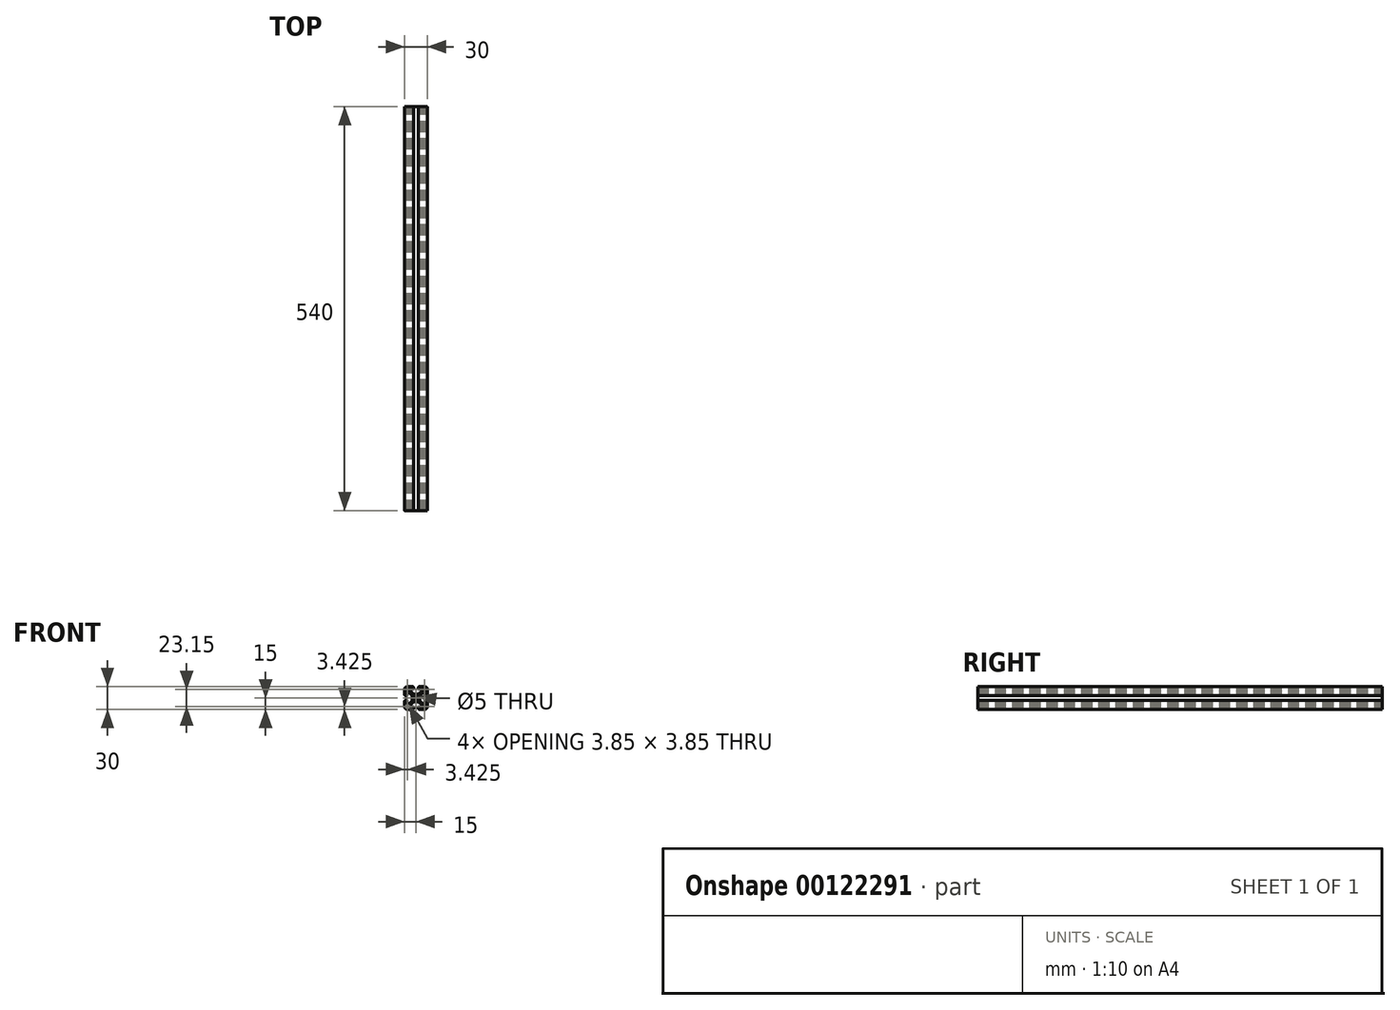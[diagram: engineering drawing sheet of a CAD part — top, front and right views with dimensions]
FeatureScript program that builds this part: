
annotation { "Feature Type Name" : "Feature", "Feature Type Description" : "" }
export const myFeature = defineFeature(function(context is Context, id is Id, definition is map)
    precondition{}
    {
        {
            var Q0;
            Q0=qCreatedBy(makeId("Front.planeOp"),FACE);
            var sketch = newSketch(context, id + "F0", { "sketchPlane" : qUnion([Q0])});
            skLineSegment(sketch, "E0", {"start": v(0, 5.25) * mm, "end": v(2.6, 5.25) * mm});
            skLineSegment(sketch, "E1", {"start": v(4.71, 6.13) * mm, "end": v(7.27, 8.69) * mm});
            skLineSegment(sketch, "E2", {"start": v(8.15, 10.8) * mm, "end": v(8.15, 12.5) * mm});
            skLineSegment(sketch, "E3", {"start": v(7.15, 13.5) * mm, "end": v(5.9, 13.5) * mm});
            skLineSegment(sketch, "E4", {"start": v(5.6, 13.2) * mm, "end": v(5.6, 12.3) * mm});
            skLineSegment(sketch, "E5", {"start": v(5.3, 12) * mm, "end": v(3.9, 12) * mm});
            skLineSegment(sketch, "E6", {"start": v(3.1, 12.8) * mm, "end": v(3.1, 14) * mm});
            skLineSegment(sketch, "E7", {"start": v(4.1, 15) * mm, "end": v(12, 15) * mm});
            skPoint(sketch, "E8.visualSharp", {"position": v(3.84, 5.25) * mm});
            skArc(sketch, "E8.filletArc", {"start": v(2.6, 5.25) * mm, "mid": v(3.74, 5.48) * mm, "end": v(4.71, 6.13) * mm});
            skPoint(sketch, "E9.visualSharp", {"position": v(8.15, 9.56) * mm});
            skArc(sketch, "E9.filletArc", {"start": v(7.27, 8.69) * mm, "mid": v(7.92, 9.66) * mm, "end": v(8.15, 10.8) * mm});
            skPoint(sketch, "E10.visualSharp", {"position": v(8.15, 13.5) * mm});
            skArc(sketch, "E10.filletArc", {"start": v(8.15, 12.5) * mm, "mid": v(7.86, 13.2) * mm, "end": v(7.15, 13.5) * mm});
            skPoint(sketch, "E11.visualSharp", {"position": v(5.6, 13.5) * mm});
            skArc(sketch, "E11.filletArc", {"start": v(5.9, 13.5) * mm, "mid": v(5.69, 13.41) * mm, "end": v(5.6, 13.2) * mm});
            skPoint(sketch, "E12.visualSharp", {"position": v(5.6, 12) * mm});
            skArc(sketch, "E12.filletArc", {"start": v(5.3, 12) * mm, "mid": v(5.51, 12.09) * mm, "end": v(5.6, 12.3) * mm});
            skPoint(sketch, "E13.visualSharp", {"position": v(3.1, 12) * mm});
            skArc(sketch, "E13.filletArc", {"start": v(3.1, 12.8) * mm, "mid": v(3.33, 12.23) * mm, "end": v(3.9, 12) * mm});
            skPoint(sketch, "E14.visualSharp", {"position": v(3.1, 15) * mm});
            skArc(sketch, "E14.filletArc", {"start": v(4.1, 15) * mm, "mid": v(3.4, 14.7) * mm, "end": v(3.1, 14) * mm});
            skArc(sketch, "E15.MirrorCS", {"start": v(12, 5.3) * mm, "mid": v(12.09, 5.51) * mm, "end": v(12.3, 5.6) * mm});
            skArc(sketch, "E16.MirrorCS", {"start": v(13.5, 5.9) * mm, "mid": v(13.41, 5.69) * mm, "end": v(13.2, 5.6) * mm});
            skPoint(sketch, "E17.MirrorP", {"position": v(13.5, 5.6) * mm});
            skLineSegment(sketch, "E18.MirrorCS", {"start": v(5.25, 0) * mm, "end": v(5.25, 2.6) * mm});
            skLineSegment(sketch, "E19.MirrorCS", {"start": v(6.13, 4.71) * mm, "end": v(8.69, 7.27) * mm});
            skPoint(sketch, "E20.MirrorP", {"position": v(13.5, 8.15) * mm});
            skLineSegment(sketch, "E21.MirrorCS", {"start": v(10.8, 8.15) * mm, "end": v(12.5, 8.15) * mm});
            skLineSegment(sketch, "E22.MirrorCS", {"start": v(13.5, 7.15) * mm, "end": v(13.5, 5.9) * mm});
            skPoint(sketch, "E23.MirrorP", {"position": v(9.56, 8.15) * mm});
            skLineSegment(sketch, "E24.MirrorCS", {"start": v(13.2, 5.6) * mm, "end": v(12.3, 5.6) * mm});
            skArc(sketch, "E25.MirrorCS", {"start": v(15, 4.1) * mm, "mid": v(14.7, 3.4) * mm, "end": v(14, 3.1) * mm});
            skArc(sketch, "E26.MirrorCS", {"start": v(12.8, 3.1) * mm, "mid": v(12.23, 3.33) * mm, "end": v(12, 3.9) * mm});
            skPoint(sketch, "E27.MirrorP", {"position": v(12, 5.6) * mm});
            skLineSegment(sketch, "E28.MirrorCS", {"start": v(12, 5.3) * mm, "end": v(12, 3.9) * mm});
            skPoint(sketch, "E29.MirrorP", {"position": v(5.25, 3.84) * mm});
            skLineSegment(sketch, "E30.MirrorCS", {"start": v(15, 4.1) * mm, "end": v(15, 12) * mm});
            skLineSegment(sketch, "E31.MirrorCS", {"start": v(12.8, 3.1) * mm, "end": v(14, 3.1) * mm});
            skArc(sketch, "E32.MirrorCS", {"start": v(5.25, 2.6) * mm, "mid": v(5.48, 3.74) * mm, "end": v(6.13, 4.71) * mm});
            skArc(sketch, "E33.MirrorCS", {"start": v(12.5, 8.15) * mm, "mid": v(13.2, 7.86) * mm, "end": v(13.5, 7.15) * mm});
            skArc(sketch, "E34.MirrorCS", {"start": v(8.69, 7.27) * mm, "mid": v(9.66, 7.92) * mm, "end": v(10.8, 8.15) * mm});
            skPoint(sketch, "E35.MirrorP", {"position": v(15, 3.1) * mm});
            skPoint(sketch, "E36.MirrorP", {"position": v(12, 3.1) * mm});
            skArc(sketch, "E37.MirrorCS", {"start": v(-5.9, 13.5) * mm, "mid": v(-5.69, 13.41) * mm, "end": v(-5.6, 13.2) * mm});
            skLineSegment(sketch, "E38.MirrorCS", {"start": v(-5.6, 13.2) * mm, "end": v(-5.6, 12.3) * mm});
            skArc(sketch, "E39.MirrorCS", {"start": v(-5.3, 12) * mm, "mid": v(-5.51, 12.09) * mm, "end": v(-5.6, 12.3) * mm});
            skArc(sketch, "E40.MirrorCS", {"start": v(-12, 5.3) * mm, "mid": v(-12.09, 5.51) * mm, "end": v(-12.3, 5.6) * mm});
            skLineSegment(sketch, "E41.MirrorCS", {"start": v(-13.2, 5.6) * mm, "end": v(-12.3, 5.6) * mm});
            skArc(sketch, "E42.MirrorCS", {"start": v(-13.5, 5.9) * mm, "mid": v(-13.41, 5.69) * mm, "end": v(-13.2, 5.6) * mm});
            skArc(sketch, "E43.MirrorCS", {"start": v(-12.5, 8.15) * mm, "mid": v(-13.2, 7.86) * mm, "end": v(-13.5, 7.15) * mm});
            skArc(sketch, "E44.MirrorCS", {"start": v(-15, 4.1) * mm, "mid": v(-14.7, 3.4) * mm, "end": v(-14, 3.1) * mm});
            skArc(sketch, "E45.MirrorCS", {"start": v(-8.15, 12.5) * mm, "mid": v(-7.86, 13.2) * mm, "end": v(-7.15, 13.5) * mm});
            skLineSegment(sketch, "E46.MirrorCS", {"start": v(-5.3, 12) * mm, "end": v(-3.9, 12) * mm});
            skLineSegment(sketch, "E47.MirrorCS", {"start": v(-7.15, 13.5) * mm, "end": v(-5.9, 13.5) * mm});
            skArc(sketch, "E48.MirrorCS", {"start": v(-3.1, 12.8) * mm, "mid": v(-3.33, 12.23) * mm, "end": v(-3.9, 12) * mm});
            skArc(sketch, "E49.MirrorCS", {"start": v(-4.1, 15) * mm, "mid": v(-3.4, 14.7) * mm, "end": v(-3.1, 14) * mm});
            skArc(sketch, "E50.MirrorCS", {"start": v(-12.8, 3.1) * mm, "mid": v(-12.23, 3.33) * mm, "end": v(-12, 3.9) * mm});
            skPoint(sketch, "E51.MirrorP", {"position": v(-12, 3.1) * mm});
            skLineSegment(sketch, "E52.MirrorCS", {"start": v(-5.25, 0) * mm, "end": v(-5.25, 2.6) * mm});
            skLineSegment(sketch, "E53.MirrorCS", {"start": v(-10.8, 8.15) * mm, "end": v(-12.5, 8.15) * mm});
            skPoint(sketch, "E54.MirrorP", {"position": v(-9.56, 8.15) * mm});
            skLineSegment(sketch, "E55.MirrorCS", {"start": v(-12, 5.3) * mm, "end": v(-12, 3.9) * mm});
            skLineSegment(sketch, "E56.MirrorCS", {"start": v(-12.8, 3.1) * mm, "end": v(-14, 3.1) * mm});
            skArc(sketch, "E57.MirrorCS", {"start": v(-7.27, 8.69) * mm, "mid": v(-7.92, 9.66) * mm, "end": v(-8.15, 10.8) * mm});
            skArc(sketch, "E58.MirrorCS", {"start": v(-2.6, 5.25) * mm, "mid": v(-3.74, 5.48) * mm, "end": v(-4.71, 6.13) * mm});
            skLineSegment(sketch, "E59.MirrorCS", {"start": v(-4.1, 15) * mm, "end": v(-12, 15) * mm});
            skLineSegment(sketch, "E60.MirrorCS", {"start": v(-3.1, 12.8) * mm, "end": v(-3.1, 14) * mm});
            skPoint(sketch, "E61.MirrorP", {"position": v(-8.15, 9.56) * mm});
            skPoint(sketch, "E62.MirrorP", {"position": v(-8.15, 13.5) * mm});
            skPoint(sketch, "E63.MirrorP", {"position": v(-5.25, 3.84) * mm});
            skLineSegment(sketch, "E64.MirrorCS", {"start": v(-8.15, 10.8) * mm, "end": v(-8.15, 12.5) * mm});
            skPoint(sketch, "E65.MirrorP", {"position": v(-15, 3.1) * mm});
            skPoint(sketch, "E66.MirrorP", {"position": v(-5.6, 13.5) * mm});
            skPoint(sketch, "E67.MirrorP", {"position": v(-3.1, 15) * mm});
            skLineSegment(sketch, "E68.MirrorCS", {"start": v(-6.13, 4.71) * mm, "end": v(-8.69, 7.27) * mm});
            skLineSegment(sketch, "E69.MirrorCS", {"start": v(-4.71, 6.13) * mm, "end": v(-7.27, 8.69) * mm});
            skArc(sketch, "E70.MirrorCS", {"start": v(-8.69, 7.27) * mm, "mid": v(-9.66, 7.92) * mm, "end": v(-10.8, 8.15) * mm});
            skLineSegment(sketch, "E71.MirrorCS", {"start": v(-13.5, 7.15) * mm, "end": v(-13.5, 5.9) * mm});
            skPoint(sketch, "E72.MirrorP", {"position": v(-13.5, 8.15) * mm});
            skPoint(sketch, "E73.MirrorP", {"position": v(-3.1, 12) * mm});
            skPoint(sketch, "E74.MirrorP", {"position": v(-3.84, 5.25) * mm});
            skPoint(sketch, "E75.MirrorP", {"position": v(-5.6, 12) * mm});
            skLineSegment(sketch, "E76.MirrorCS", {"start": v(0, 5.25) * mm, "end": v(-2.6, 5.25) * mm});
            skLineSegment(sketch, "E77.MirrorCS", {"start": v(-15, 4.1) * mm, "end": v(-15, 12) * mm});
            skArc(sketch, "E78.MirrorCS", {"start": v(-5.25, 2.6) * mm, "mid": v(-5.48, 3.74) * mm, "end": v(-6.13, 4.71) * mm});
            skPoint(sketch, "E79.MirrorP", {"position": v(-12, 5.6) * mm});
            skPoint(sketch, "E80.MirrorP", {"position": v(-13.5, 5.6) * mm});
            skLineSegment(sketch, "E81.MirrorCS", {"start": v(5.6, -13.2) * mm, "end": v(5.6, -12.3) * mm});
            skArc(sketch, "E82.MirrorCS", {"start": v(5.9, -13.5) * mm, "mid": v(5.69, -13.41) * mm, "end": v(5.6, -13.2) * mm});
            skArc(sketch, "E83.MirrorCS", {"start": v(5.3, -12) * mm, "mid": v(5.51, -12.09) * mm, "end": v(5.6, -12.3) * mm});
            skArc(sketch, "E84.MirrorCS", {"start": v(-12, -5.3) * mm, "mid": v(-12.09, -5.51) * mm, "end": v(-12.3, -5.6) * mm});
            skArc(sketch, "E85.MirrorCS", {"start": v(-5.9, -13.5) * mm, "mid": v(-5.69, -13.41) * mm, "end": v(-5.6, -13.2) * mm});
            skLineSegment(sketch, "E86.MirrorCS", {"start": v(13.2, -5.6) * mm, "end": v(12.3, -5.6) * mm});
            skArc(sketch, "E87.MirrorCS", {"start": v(-5.3, -12) * mm, "mid": v(-5.51, -12.09) * mm, "end": v(-5.6, -12.3) * mm});
            skArc(sketch, "E88.MirrorCS", {"start": v(13.5, -5.9) * mm, "mid": v(13.41, -5.69) * mm, "end": v(13.2, -5.6) * mm});
            skLineSegment(sketch, "E89.MirrorCS", {"start": v(-5.6, -13.2) * mm, "end": v(-5.6, -12.3) * mm});
            skArc(sketch, "E90.MirrorCS", {"start": v(-13.5, -5.9) * mm, "mid": v(-13.41, -5.69) * mm, "end": v(-13.2, -5.6) * mm});
            skArc(sketch, "E91.MirrorCS", {"start": v(12, -5.3) * mm, "mid": v(12.09, -5.51) * mm, "end": v(12.3, -5.6) * mm});
            skLineSegment(sketch, "E92.MirrorCS", {"start": v(-13.2, -5.6) * mm, "end": v(-12.3, -5.6) * mm});
            skArc(sketch, "E93.MirrorCS", {"start": v(-15, -4.1) * mm, "mid": v(-14.7, -3.4) * mm, "end": v(-14, -3.1) * mm});
            skArc(sketch, "E94.MirrorCS", {"start": v(-12.5, -8.15) * mm, "mid": v(-13.2, -7.86) * mm, "end": v(-13.5, -7.15) * mm});
            skArc(sketch, "E95.MirrorCS", {"start": v(12.8, -3.1) * mm, "mid": v(12.23, -3.33) * mm, "end": v(12, -3.9) * mm});
            skArc(sketch, "E96.MirrorCS", {"start": v(-12.8, -3.1) * mm, "mid": v(-12.23, -3.33) * mm, "end": v(-12, -3.9) * mm});
            skLineSegment(sketch, "E97.MirrorCS", {"start": v(7.15, -13.5) * mm, "end": v(5.9, -13.5) * mm});
            skLineSegment(sketch, "E98.MirrorCS", {"start": v(5.3, -12) * mm, "end": v(3.9, -12) * mm});
            skArc(sketch, "E99.MirrorCS", {"start": v(8.15, -12.5) * mm, "mid": v(7.86, -13.2) * mm, "end": v(7.15, -13.5) * mm});
            skArc(sketch, "E100.MirrorCS", {"start": v(-4.1, -15) * mm, "mid": v(-3.4, -14.7) * mm, "end": v(-3.1, -14) * mm});
            skArc(sketch, "E101.MirrorCS", {"start": v(-3.1, -12.8) * mm, "mid": v(-3.33, -12.23) * mm, "end": v(-3.9, -12) * mm});
            skArc(sketch, "E102.MirrorCS", {"start": v(15, -4.1) * mm, "mid": v(14.7, -3.4) * mm, "end": v(14, -3.1) * mm});
            skArc(sketch, "E103.MirrorCS", {"start": v(-8.15, -12.5) * mm, "mid": v(-7.86, -13.2) * mm, "end": v(-7.15, -13.5) * mm});
            skArc(sketch, "E104.MirrorCS", {"start": v(12.5, -8.15) * mm, "mid": v(13.2, -7.86) * mm, "end": v(13.5, -7.15) * mm});
            skArc(sketch, "E105.MirrorCS", {"start": v(3.1, -12.8) * mm, "mid": v(3.33, -12.23) * mm, "end": v(3.9, -12) * mm});
            skArc(sketch, "E106.MirrorCS", {"start": v(4.1, -15) * mm, "mid": v(3.4, -14.7) * mm, "end": v(3.1, -14) * mm});
            skPoint(sketch, "E107.MirrorP", {"position": v(-3.1, -15) * mm});
            skArc(sketch, "E108.MirrorCS", {"start": v(-2.6, -5.25) * mm, "mid": v(-3.74, -5.48) * mm, "end": v(-4.71, -6.13) * mm});
            skLineSegment(sketch, "E109.MirrorCS", {"start": v(5.25, 0) * mm, "end": v(5.25, -2.6) * mm});
            skLineSegment(sketch, "E110.MirrorCS", {"start": v(-6.13, -4.71) * mm, "end": v(-8.69, -7.27) * mm});
            skLineSegment(sketch, "E111.MirrorCS", {"start": v(-12, -5.3) * mm, "end": v(-12, -3.9) * mm});
            skLineSegment(sketch, "E112.MirrorCS", {"start": v(12, -5.3) * mm, "end": v(12, -3.9) * mm});
            skLineSegment(sketch, "E113.MirrorCS", {"start": v(-7.15, -13.5) * mm, "end": v(-5.9, -13.5) * mm});
            skLineSegment(sketch, "E114.MirrorCS", {"start": v(-13.5, -7.15) * mm, "end": v(-13.5, -5.9) * mm});
            skPoint(sketch, "E115.MirrorP", {"position": v(5.6, -12) * mm});
            skPoint(sketch, "E116.MirrorP", {"position": v(12, -5.6) * mm});
            skPoint(sketch, "E117.MirrorP", {"position": v(-5.25, -3.84) * mm});
            skPoint(sketch, "E118.MirrorP", {"position": v(3.1, -15) * mm});
            skPoint(sketch, "E119.MirrorP", {"position": v(-5.6, -13.5) * mm});
            skArc(sketch, "E120.MirrorCS", {"start": v(-7.27, -8.69) * mm, "mid": v(-7.92, -9.66) * mm, "end": v(-8.15, -10.8) * mm});
            skPoint(sketch, "E121.MirrorP", {"position": v(8.15, -9.56) * mm});
            skPoint(sketch, "E122.MirrorP", {"position": v(9.56, -8.15) * mm});
            skPoint(sketch, "E123.MirrorP", {"position": v(-3.1, -12) * mm});
            skArc(sketch, "E124.MirrorCS", {"start": v(8.69, -7.27) * mm, "mid": v(9.66, -7.92) * mm, "end": v(10.8, -8.15) * mm});
            skLineSegment(sketch, "E125.MirrorCS", {"start": v(-8.15, -10.8) * mm, "end": v(-8.15, -12.5) * mm});
            skLineSegment(sketch, "E126.MirrorCS", {"start": v(-10.8, -8.15) * mm, "end": v(-12.5, -8.15) * mm});
            skLineSegment(sketch, "E127.MirrorCS", {"start": v(13.5, -7.15) * mm, "end": v(13.5, -5.9) * mm});
            skPoint(sketch, "E128.MirrorP", {"position": v(-9.56, -8.15) * mm});
            skPoint(sketch, "E129.MirrorP", {"position": v(-13.5, -5.6) * mm});
            skLineSegment(sketch, "E130.MirrorCS", {"start": v(-5.3, -12) * mm, "end": v(-3.9, -12) * mm});
            skArc(sketch, "E131.MirrorCS", {"start": v(-8.69, -7.27) * mm, "mid": v(-9.66, -7.92) * mm, "end": v(-10.8, -8.15) * mm});
            skArc(sketch, "E132.MirrorCS", {"start": v(5.25, -2.6) * mm, "mid": v(5.48, -3.74) * mm, "end": v(6.13, -4.71) * mm});
            skArc(sketch, "E133.MirrorCS", {"start": v(-5.25, -2.6) * mm, "mid": v(-5.48, -3.74) * mm, "end": v(-6.13, -4.71) * mm});
            skPoint(sketch, "E134.MirrorP", {"position": v(12, -3.1) * mm});
            skPoint(sketch, "E135.MirrorP", {"position": v(-8.15, -13.5) * mm});
            skPoint(sketch, "E136.MirrorP", {"position": v(-5.6, -12) * mm});
            skPoint(sketch, "E137.MirrorP", {"position": v(8.15, -13.5) * mm});
            skPoint(sketch, "E138.MirrorP", {"position": v(-3.84, -5.25) * mm});
            skPoint(sketch, "E139.MirrorP", {"position": v(-8.15, -9.56) * mm});
            skPoint(sketch, "E140.MirrorP", {"position": v(15, -3.1) * mm});
            skLineSegment(sketch, "E141.MirrorCS", {"start": v(3.1, -12.8) * mm, "end": v(3.1, -14) * mm});
            skLineSegment(sketch, "E142.MirrorCS", {"start": v(4.1, -15) * mm, "end": v(12, -15) * mm});
            skArc(sketch, "E143.MirrorCS", {"start": v(2.6, -5.25) * mm, "mid": v(3.74, -5.48) * mm, "end": v(4.71, -6.13) * mm});
            skArc(sketch, "E144.MirrorCS", {"start": v(7.27, -8.69) * mm, "mid": v(7.92, -9.66) * mm, "end": v(8.15, -10.8) * mm});
            skPoint(sketch, "E145.MirrorP", {"position": v(-15, -3.1) * mm});
            skLineSegment(sketch, "E146.MirrorCS", {"start": v(-15, -4.1) * mm, "end": v(-15, -12) * mm});
            skLineSegment(sketch, "E147.MirrorCS", {"start": v(0, -5.25) * mm, "end": v(-2.6, -5.25) * mm});
            skLineSegment(sketch, "E148.MirrorCS", {"start": v(15, -4.1) * mm, "end": v(15, -12) * mm});
            skLineSegment(sketch, "E149.MirrorCS", {"start": v(12.8, -3.1) * mm, "end": v(14, -3.1) * mm});
            skLineSegment(sketch, "E150.MirrorCS", {"start": v(-4.71, -6.13) * mm, "end": v(-7.27, -8.69) * mm});
            skPoint(sketch, "E151.MirrorP", {"position": v(5.6, -13.5) * mm});
            skPoint(sketch, "E152.MirrorP", {"position": v(-12, -5.6) * mm});
            skPoint(sketch, "E153.MirrorP", {"position": v(5.25, -3.84) * mm});
            skPoint(sketch, "E154.MirrorP", {"position": v(-12, -3.1) * mm});
            skLineSegment(sketch, "E155.MirrorCS", {"start": v(10.8, -8.15) * mm, "end": v(12.5, -8.15) * mm});
            skPoint(sketch, "E156.MirrorP", {"position": v(3.84, -5.25) * mm});
            skPoint(sketch, "E157.MirrorP", {"position": v(13.5, -5.6) * mm});
            skPoint(sketch, "E158.MirrorP", {"position": v(-13.5, -8.15) * mm});
            skPoint(sketch, "E159.MirrorP", {"position": v(13.5, -8.15) * mm});
            skLineSegment(sketch, "E160.MirrorCS", {"start": v(0, -5.25) * mm, "end": v(2.6, -5.25) * mm});
            skLineSegment(sketch, "E161.MirrorCS", {"start": v(6.13, -4.71) * mm, "end": v(8.69, -7.27) * mm});
            skLineSegment(sketch, "E162.MirrorCS", {"start": v(-3.1, -12.8) * mm, "end": v(-3.1, -14) * mm});
            skLineSegment(sketch, "E163.MirrorCS", {"start": v(-5.25, 0) * mm, "end": v(-5.25, -2.6) * mm});
            skLineSegment(sketch, "E164.MirrorCS", {"start": v(-4.1, -15) * mm, "end": v(-12, -15) * mm});
            skLineSegment(sketch, "E165.MirrorCS", {"start": v(4.71, -6.13) * mm, "end": v(7.27, -8.69) * mm});
            skLineSegment(sketch, "E166.MirrorCS", {"start": v(-12.8, -3.1) * mm, "end": v(-14, -3.1) * mm});
            skLineSegment(sketch, "E167.MirrorCS", {"start": v(8.15, -10.8) * mm, "end": v(8.15, -12.5) * mm});
            skPoint(sketch, "E168.MirrorP", {"position": v(3.1, -12) * mm});
            skCircle(sketch, "E169", {"center": v(0, 0) * mm, "radius": 2.5 * mm});
            skLineSegment(sketch, "E170.bottom", {"start": v(9.95, 13.5) * mm, "end": v(12, 13.5) * mm});
            skLineSegment(sketch, "E170.top", {"start": v(9.95, 9.65) * mm, "end": v(13.2, 9.65) * mm});
            skLineSegment(sketch, "E170.left", {"start": v(9.65, 13.2) * mm, "end": v(9.65, 9.95) * mm});
            skLineSegment(sketch, "E170.right", {"start": v(13.5, 12) * mm, "end": v(13.5, 9.95) * mm});
            skPoint(sketch, "E171.visualSharp", {"position": v(9.65, 9.65) * mm});
            skArc(sketch, "E171.filletArc", {"start": v(9.65, 9.95) * mm, "mid": v(9.74, 9.74) * mm, "end": v(9.95, 9.65) * mm});
            skPoint(sketch, "E172.visualSharp", {"position": v(13.5, 9.65) * mm});
            skArc(sketch, "E172.filletArc", {"start": v(13.2, 9.65) * mm, "mid": v(13.41, 9.74) * mm, "end": v(13.5, 9.95) * mm});
            skPoint(sketch, "E173.visualSharp", {"position": v(9.65, 13.5) * mm});
            skArc(sketch, "E173.filletArc", {"start": v(9.95, 13.5) * mm, "mid": v(9.74, 13.41) * mm, "end": v(9.65, 13.2) * mm});
            skPoint(sketch, "E174.visualSharp", {"position": v(13.5, 13.5) * mm});
            skArc(sketch, "E174.filletArc", {"start": v(13.5, 12) * mm, "mid": v(13.06, 13.06) * mm, "end": v(12, 13.5) * mm});
            skArc(sketch, "E175.MirrorCS", {"start": v(-13.2, 9.65) * mm, "mid": v(-13.41, 9.74) * mm, "end": v(-13.5, 9.95) * mm});
            skArc(sketch, "E176.MirrorCS", {"start": v(-9.65, 9.95) * mm, "mid": v(-9.74, 9.74) * mm, "end": v(-9.95, 9.65) * mm});
            skArc(sketch, "E177.MirrorCS", {"start": v(-9.95, 13.5) * mm, "mid": v(-9.74, 13.41) * mm, "end": v(-9.65, 13.2) * mm});
            skPoint(sketch, "E178.MirrorP", {"position": v(-13.5, 9.65) * mm});
            skPoint(sketch, "E179.MirrorP", {"position": v(-9.65, 9.65) * mm});
            skArc(sketch, "E180.MirrorCS", {"start": v(-13.5, 12) * mm, "mid": v(-13.06, 13.06) * mm, "end": v(-12, 13.5) * mm});
            skLineSegment(sketch, "E181.MirrorCS", {"start": v(-13.5, 12) * mm, "end": v(-13.5, 9.95) * mm});
            skLineSegment(sketch, "E182.MirrorCS", {"start": v(-9.95, 13.5) * mm, "end": v(-12, 13.5) * mm});
            skPoint(sketch, "E183.MirrorP", {"position": v(-13.5, 13.5) * mm});
            skPoint(sketch, "E184.MirrorP", {"position": v(-9.65, 13.5) * mm});
            skLineSegment(sketch, "E185.MirrorCS", {"start": v(-9.95, 9.65) * mm, "end": v(-13.2, 9.65) * mm});
            skLineSegment(sketch, "E186.MirrorCS", {"start": v(-9.65, 13.2) * mm, "end": v(-9.65, 9.95) * mm});
            skArc(sketch, "E187.MirrorCS", {"start": v(-9.65, -9.95) * mm, "mid": v(-9.74, -9.74) * mm, "end": v(-9.95, -9.65) * mm});
            skArc(sketch, "E188.MirrorCS", {"start": v(-9.95, -13.5) * mm, "mid": v(-9.74, -13.41) * mm, "end": v(-9.65, -13.2) * mm});
            skArc(sketch, "E189.MirrorCS", {"start": v(-13.2, -9.65) * mm, "mid": v(-13.41, -9.74) * mm, "end": v(-13.5, -9.95) * mm});
            skArc(sketch, "E190.MirrorCS", {"start": v(-13.5, -12) * mm, "mid": v(-13.06, -13.06) * mm, "end": v(-12, -13.5) * mm});
            skLineSegment(sketch, "E191.MirrorCS", {"start": v(-13.5, -12) * mm, "end": v(-13.5, -9.95) * mm});
            skLineSegment(sketch, "E192.MirrorCS", {"start": v(-9.95, -13.5) * mm, "end": v(-12, -13.5) * mm});
            skLineSegment(sketch, "E193.MirrorCS", {"start": v(-9.95, -9.65) * mm, "end": v(-13.2, -9.65) * mm});
            skLineSegment(sketch, "E194.MirrorCS", {"start": v(-9.65, -13.2) * mm, "end": v(-9.65, -9.95) * mm});
            skPoint(sketch, "E195.MirrorP", {"position": v(-9.65, -13.5) * mm});
            skPoint(sketch, "E196.MirrorP", {"position": v(-13.5, -13.5) * mm});
            skPoint(sketch, "E197.MirrorP", {"position": v(-9.65, -9.65) * mm});
            skPoint(sketch, "E198.MirrorP", {"position": v(-13.5, -9.65) * mm});
            skArc(sketch, "E199.MirrorCS", {"start": v(9.95, -13.5) * mm, "mid": v(9.74, -13.41) * mm, "end": v(9.65, -13.2) * mm});
            skArc(sketch, "E200.MirrorCS", {"start": v(9.65, -9.95) * mm, "mid": v(9.74, -9.74) * mm, "end": v(9.95, -9.65) * mm});
            skArc(sketch, "E201.MirrorCS", {"start": v(13.2, -9.65) * mm, "mid": v(13.41, -9.74) * mm, "end": v(13.5, -9.95) * mm});
            skPoint(sketch, "E202.MirrorP", {"position": v(9.65, -13.5) * mm});
            skPoint(sketch, "E203.MirrorP", {"position": v(9.65, -9.65) * mm});
            skPoint(sketch, "E204.MirrorP", {"position": v(13.5, -9.65) * mm});
            skPoint(sketch, "E205.MirrorP", {"position": v(13.5, -13.5) * mm});
            skLineSegment(sketch, "E206.MirrorCS", {"start": v(9.95, -13.5) * mm, "end": v(12, -13.5) * mm});
            skLineSegment(sketch, "E207.MirrorCS", {"start": v(9.95, -9.65) * mm, "end": v(13.2, -9.65) * mm});
            skLineSegment(sketch, "E208.MirrorCS", {"start": v(13.5, -12) * mm, "end": v(13.5, -9.95) * mm});
            skLineSegment(sketch, "E209.MirrorCS", {"start": v(9.65, -13.2) * mm, "end": v(9.65, -9.95) * mm});
            skArc(sketch, "E210.MirrorCS", {"start": v(13.5, -12) * mm, "mid": v(13.06, -13.06) * mm, "end": v(12, -13.5) * mm});
            skPoint(sketch, "E211.visualSharp", {"position": v(15, 15) * mm});
            skArc(sketch, "E211.filletArc", {"start": v(15, 12) * mm, "mid": v(14.12, 14.12) * mm, "end": v(12, 15) * mm});
            skPoint(sketch, "E212.visualSharp", {"position": v(15, -15) * mm});
            skArc(sketch, "E212.filletArc", {"start": v(12, -15) * mm, "mid": v(14.12, -14.12) * mm, "end": v(15, -12) * mm});
            skPoint(sketch, "E213.visualSharp", {"position": v(-15, -15) * mm});
            skArc(sketch, "E213.filletArc", {"start": v(-15, -12) * mm, "mid": v(-14.12, -14.12) * mm, "end": v(-12, -15) * mm});
            skPoint(sketch, "E214.visualSharp", {"position": v(-15, 15) * mm});
            skArc(sketch, "E214.filletArc", {"start": v(-12, 15) * mm, "mid": v(-14.12, 14.12) * mm, "end": v(-15, 12) * mm});
            skSolve(sketch);
        }
        {
            var Q0;
            Q0 = qSketchRegion(id + "F0", true);
            extrude(context, id + "F1", {"entities" : qUnion([Q0]), "depth" : 540 * mm});
        }
    });
